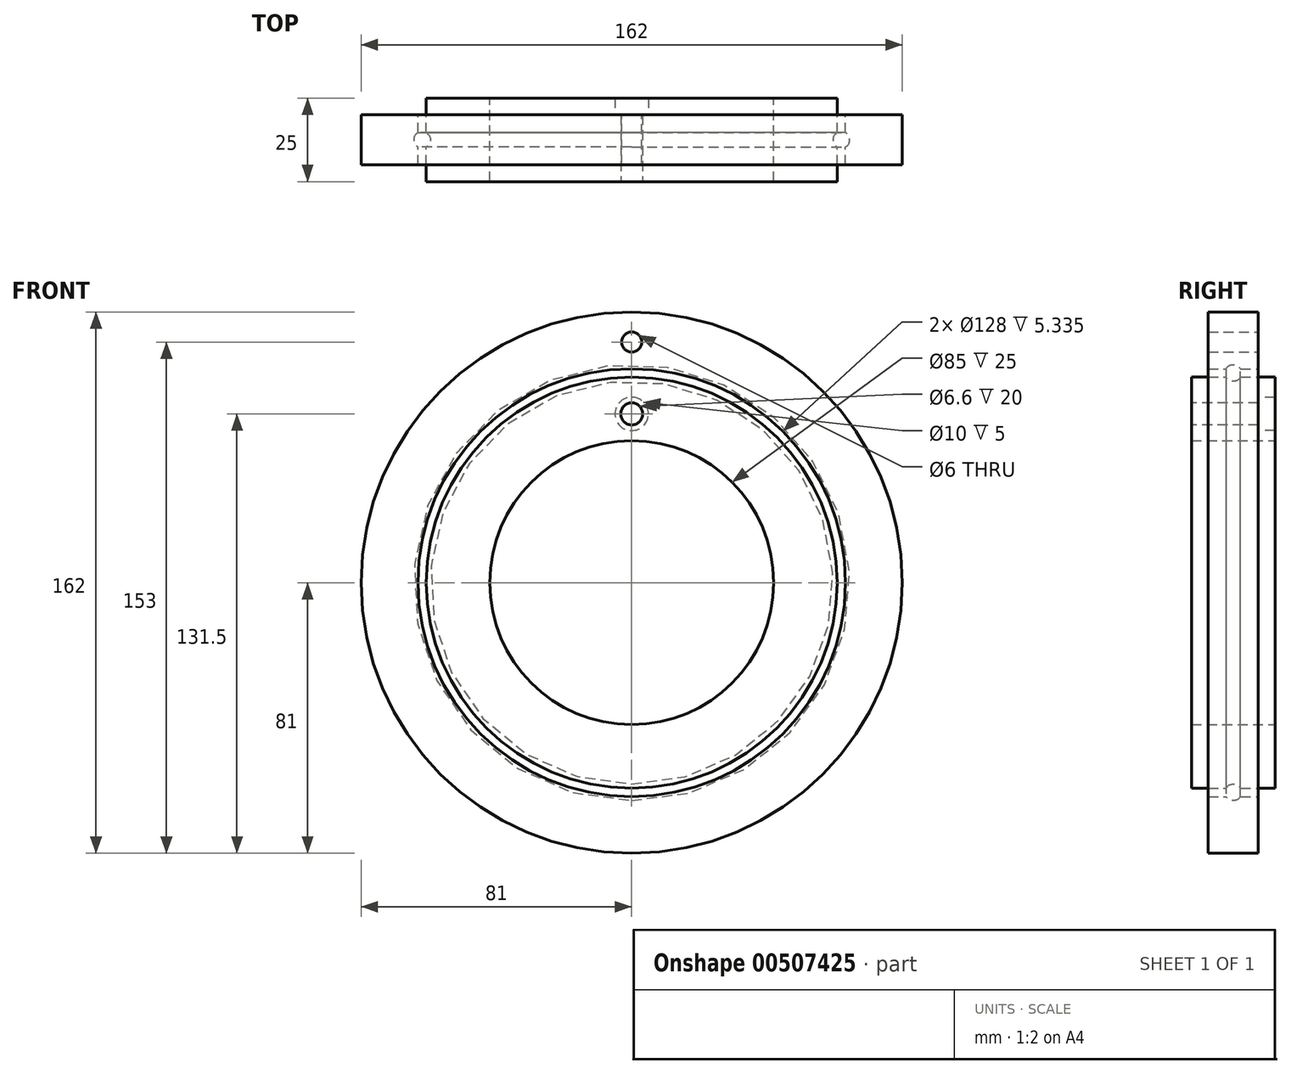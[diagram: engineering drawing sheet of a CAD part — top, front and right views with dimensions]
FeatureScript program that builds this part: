
annotation { "Feature Type Name" : "Feature", "Feature Type Description" : "" }
export const myFeature = defineFeature(function(context is Context, id is Id, definition is map)
    precondition{}
    {
        {
            var Q0;
            Q0=qCreatedBy(makeId("Front.planeOp"),FACE);
            var sketch = newSketch(context, id + "F0", { "sketchPlane" : qUnion([Q0])});
            skCircle(sketch, "E0", {"center": v(0, 0) * mm, "radius": 81 * mm});
            skCircle(sketch, "E1", {"center": v(0, 0) * mm, "radius": 64 * mm});
            skSolve(sketch);
        }
        {
            var Q0;
            Q0=makeQuery(id+"F0.imprint","IMPRINT",FACE,{"disambiguationData":[TD([[makeQuery(id+"F0.imprint","IMPRINT",EDGE,{"derivedFrom":sQuery(id+"F0.wireOp",EDGE,"E0")}),1.0]])]});
            extrude(context, id + "F1", {"entities" : qUnion([Q0]), "depth" : 15 * mm, "offsetDistance" : 25 * mm, "symmetric" : true});
        }
        {
            var Q0;
            Q0=qCreatedBy(makeId("Front.planeOp"),FACE);
            var sketch = newSketch(context, id + "F2", { "sketchPlane" : qUnion([Q0])});
            skCircle(sketch, "E2", {"center": v(0, 0) * mm, "radius": 61.5 * mm});
            skCircle(sketch, "E3", {"center": v(0, 0) * mm, "radius": 42.5 * mm});
            skSolve(sketch);
        }
        {
            var Q0;
            Q0=makeQuery(id+"F2.imprint","IMPRINT",FACE,{"disambiguationData":[TD([[makeQuery(id+"F2.imprint","IMPRINT",EDGE,{"derivedFrom":sQuery(id+"F2.wireOp",EDGE,"E2")}),1.0]])]});
            extrude(context, id + "F3", {"entities" : qUnion([Q0]), "depth" : 25 * mm, "offsetDistance" : 25 * mm, "symmetric" : true});
        }
        {
            var Q0;
            Q0=qCreatedBy(makeId("Right.planeOp"),FACE);
            var sketch = newSketch(context, id + "F4", { "sketchPlane" : qUnion([Q0])});
            skCircle(sketch, "E4", {"center": v(0, 62.75) * mm, "radius": 2.5 * mm});
            skSolve(sketch);
        }
        {
            var Q0;
            Q0 = qSketchRegion(id + "F4", true);
            var Q1;
            Q1=makeQuery(id+"F3.opExtrude","SWEPT_FACE",FACE,{"disambiguationData":[OSD([sQuery(id+"F2.wireOp",EDGE,"E3")])]});
            revolve(context, id + "F5", {"operationType" : NewBodyOperationType.REMOVE, "entities" : qUnion([Q0]), "axis" : qUnion([Q1]), "revolveType" : RevolveType.FULL, "oppositeDirection" : true});
        }
        {
            var Q0;
            Q0=makeQuery(id+"F3.opExtrude","CAP_FACE",FACE,{"disambiguationData":[OSD([sQuery(id+"F2.wireOp",EDGE,"E2"),sQuery(id+"F2.wireOp",EDGE,"E3")])],"isStart":true});
            var sketch = newSketch(context, id + "F6", { "sketchPlane" : qUnion([Q0])});
            skPoint(sketch, "E5", {"position": v(0, 50.5) * mm});
            skCircle(sketch, "E6", {"center": v(0, 0) * mm, "radius": 50.5 * mm, "construction": true});
            skSolve(sketch);
        }
        {
            var Q0;
            Q0=makeQuery(id+"F1.opExtrude","CAP_FACE",FACE,{"disambiguationData":[OSD([sQuery(id+"F0.wireOp",EDGE,"E0"),sQuery(id+"F0.wireOp",EDGE,"E1")])],"isStart":false});
            var sketch = newSketch(context, id + "F7", { "sketchPlane" : qUnion([Q0])});
            skPoint(sketch, "E7", {"position": v(0, 72) * mm});
            skCircle(sketch, "E8", {"center": v(0, 0) * mm, "radius": 72 * mm, "construction": true});
            skSolve(sketch);
        }
        {
            var Q0;
            Q0=sQuery(id+"F6.wireOp",VERTEX,"E5");
            var Q1;
            Q1=makeQuery(id+"F3.opExtrude","SWEPT_BODY",BODY,{"disambiguationData":[OSD([sQuery(id+"F2.wireOp",EDGE,"E2"),sQuery(id+"F2.wireOp",EDGE,"E3")])]});
            hole(context, id + "F8", {"style" : HoleStyle.C_BORE, "endStyle" : HoleEndStyle.THROUGH, "holeDiameter" : 6.6 * mm, "cBoreDiameter" : 10 * mm, "cBoreDepth" : 5 * mm, "isTappedThrough" : true, "tappedDepth" : 12 * mm, "tapClearance" : 3, "locations" : qUnion([Q0]), "scope" : qUnion([Q1]), "startStyle" : HoleStartStyle.SKETCH});
        }
        {
            var Q0;
            Q0=sQuery(id+"F7.wireOp",VERTEX,"E7");
            var Q1;
            Q1=makeQuery(id+"F1.opExtrude","SWEPT_BODY",BODY,{"disambiguationData":[OSD([sQuery(id+"F0.wireOp",EDGE,"E0"),sQuery(id+"F0.wireOp",EDGE,"E1")])]});
            hole(context, id + "F9", {"style" : HoleStyle.SIMPLE, "endStyle" : HoleEndStyle.THROUGH, "holeDiameter" : 6 * mm, "isTappedThrough" : true, "tappedDepth" : 12 * mm, "tapClearance" : 3, "locations" : qUnion([Q0]), "scope" : qUnion([Q1]), "startStyle" : HoleStartStyle.SKETCH});
        }
    });
